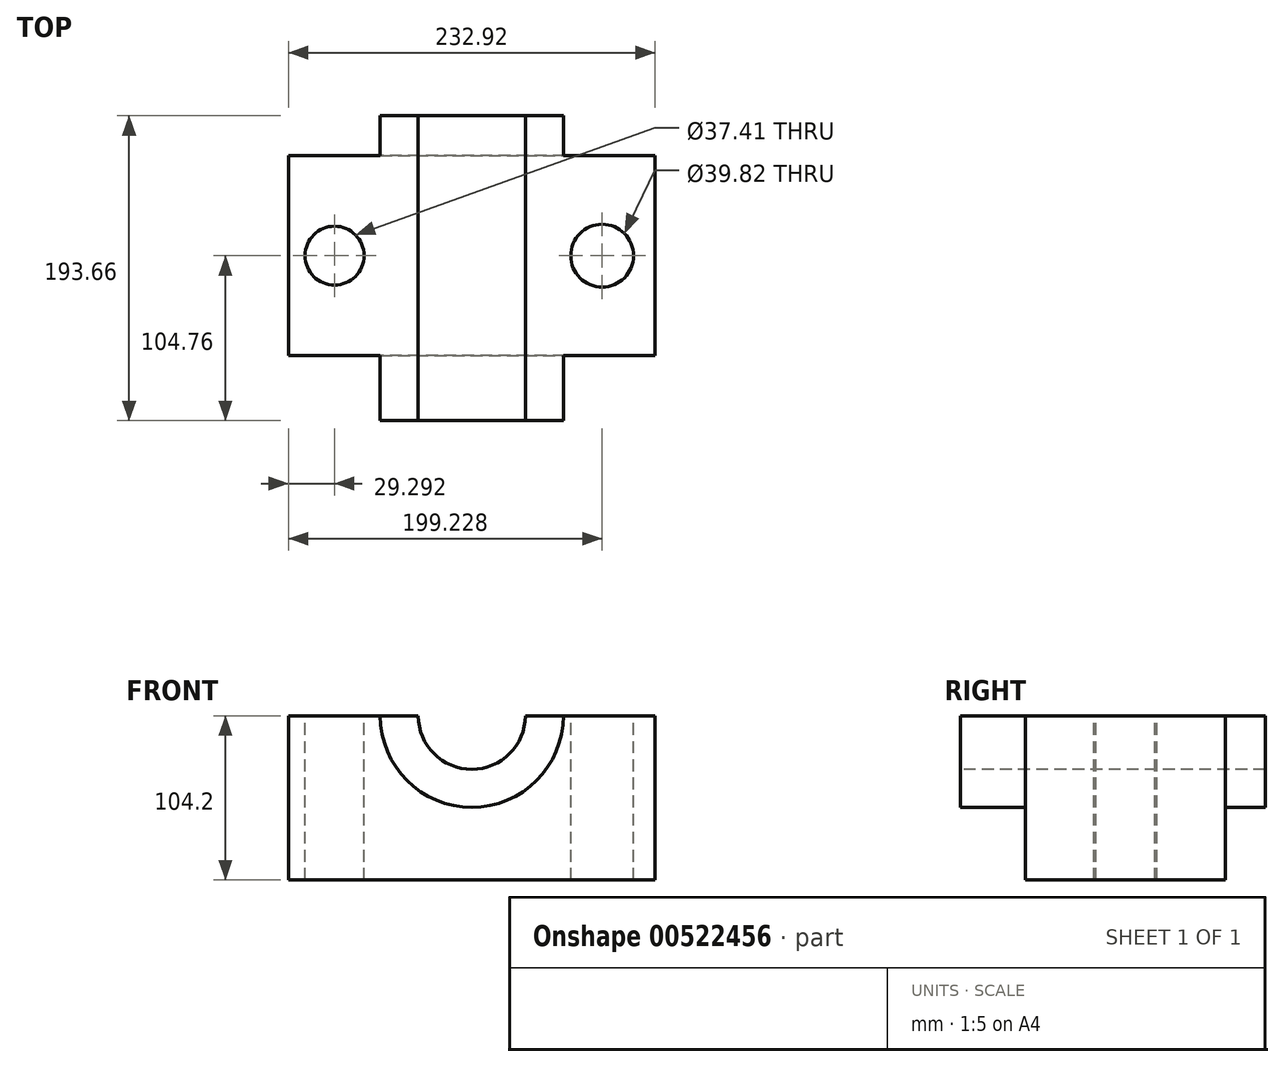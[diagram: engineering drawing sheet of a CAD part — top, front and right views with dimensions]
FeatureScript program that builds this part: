
annotation { "Feature Type Name" : "Feature", "Feature Type Description" : "" }
export const myFeature = defineFeature(function(context is Context, id is Id, definition is map)
    precondition{}
    {
        {
            var Q0;
            Q0=qCreatedBy(makeId("Front.planeOp"),FACE);
            var sketch = newSketch(context, id + "F0", { "sketchPlane" : qUnion([Q0])});
            skLineSegment(sketch, "E0.bottom", {"start": v(116.46, -52.1) * mm, "end": v(-116.46, -52.1) * mm});
            skLineSegment(sketch, "E0.top", {"start": v(116.46, 52.1) * mm, "end": v(-116.46, 52.1) * mm});
            skLineSegment(sketch, "E0.left", {"start": v(116.46, -52.1) * mm, "end": v(116.46, 52.1) * mm});
            skLineSegment(sketch, "E0.right", {"start": v(-116.46, -52.1) * mm, "end": v(-116.46, 52.1) * mm});
            skPoint(sketch, "E0.middle", {"position": v(0, 0) * mm});
            skSolve(sketch);
        }
        {
            var Q0;
            Q0 = qSketchRegion(id + "F0", true);
            extrude(context, id + "F1", {"entities" : qUnion([Q0]), "endBound" : BoundingType.SYMMETRIC, "oppositeDirection" : true, "depth" : 127 * mm, "offsetDistance" : 25.4 * mm});
        }
        {
            var Q0;
            Q0=makeQuery(id+"F1.opExtrude","CAP_FACE",FACE,{"disambiguationData":[OSD([sQuery(id+"F0.wireOp",EDGE,"E0.bottom"),sQuery(id+"F0.wireOp",EDGE,"E0.top"),sQuery(id+"F0.wireOp",EDGE,"E0.left"),sQuery(id+"F0.wireOp",EDGE,"E0.right")])],"isStart":true});
            var sketch = newSketch(context, id + "F2", { "sketchPlane" : qUnion([Q0])});
            skArc(sketch, "E1", {"start": v(-51.18, 52.1) * mm, "mid": v(0, 0.93) * mm, "end": v(51.18, 52.1) * mm});
            skArc(sketch, "E2", {"start": v(-34.02, 52.1) * mm, "mid": v(0, 18.08) * mm, "end": v(34.02, 52.1) * mm});
            skSolve(sketch);
        }
        {
            var Q0;
            Q0 = qSketchRegion(id + "F2", true);
            var Q1;
            {var subQ0=sQuery(id+"F2.wireOp",EDGE,"E2");Q1=makeQuery(id+"F2.imprint","IMPRINT",FACE,{"disambiguationData":[TD([[makeQuery(id+"F2.imprint","IMPRINT",EDGE,{"derivedFrom":subQ0}),1.0]])]});}
            extrude(context, id + "F3", {"entities" : qUnion([Q0, Q1]), "operationType" : NewBodyOperationType.REMOVE, "oppositeDirection" : true, "depth" : 296.93 * mm, "offsetDistance" : 25.4 * mm});
        }
        {
            var Q0;
            Q0=makeQuery(id+"F1.opExtrude","CAP_FACE",FACE,{"disambiguationData":[OSD([sQuery(id+"F0.wireOp",EDGE,"E0.bottom"),sQuery(id+"F0.wireOp",EDGE,"E0.top"),sQuery(id+"F0.wireOp",EDGE,"E0.left"),sQuery(id+"F0.wireOp",EDGE,"E0.right")])],"isStart":true});
            var sketch = newSketch(context, id + "F4", { "sketchPlane" : qUnion([Q0])});
            skArc(sketch, "E3", {"start": v(-58.18, 52.1) * mm, "mid": v(0, -6.08) * mm, "end": v(58.18, 52.1) * mm});
            skSolve(sketch);
        }
        {
            var Q0;
            {var subQ0=sQuery(id+"F4.wireOp",EDGE,"E3");Q0=makeQuery(id+"F4.imprint","IMPRINT",FACE,{"disambiguationData":[TD([[makeQuery(id+"F4.imprint","IMPRINT",EDGE,{"derivedFrom":subQ0}),1.0]])]});}
            extrude(context, id + "F5", {"entities" : qUnion([Q0]), "operationType" : NewBodyOperationType.ADD, "endBound" : BoundingType.SYMMETRIC, "depth" : 304.8 * mm, "offsetDistance" : 25.4 * mm});
        }
        {
            var Q0;
            Q0=qCreatedBy(makeId("Right.planeOp"),FACE);
            var sketch = newSketch(context, id + "F6", { "sketchPlane" : qUnion([Q0])});
            skLineSegment(sketch, "E4.bottom", {"start": v(-104.76, 71.05) * mm, "end": v(-229.58, 71.05) * mm});
            skLineSegment(sketch, "E4.top", {"start": v(-104.76, -42.63) * mm, "end": v(-229.58, -42.63) * mm});
            skLineSegment(sketch, "E4.left", {"start": v(-104.76, 71.05) * mm, "end": v(-104.76, -42.63) * mm});
            skLineSegment(sketch, "E4.right", {"start": v(-229.58, 71.05) * mm, "end": v(-229.58, -42.63) * mm});
            skSolve(sketch);
        }
        {
            var Q0;
            Q0 = qSketchRegion(id + "F6", true);
            extrude(context, id + "F7", {"entities" : qUnion([Q0]), "operationType" : NewBodyOperationType.REMOVE, "endBound" : BoundingType.SYMMETRIC, "oppositeDirection" : true, "depth" : 155.96 * mm, "offsetDistance" : 25.4 * mm});
        }
        {
            var Q0;
            {var subQ0=sQuery(id+"F0.wireOp",EDGE,"E0.right");var subQ2=sQuery(id+"F0.wireOp",EDGE,"E0.top");var subQ5=makeQuery(id+"F1.opExtrude","SWEPT_FACE",FACE,{"disambiguationData":[OSD([subQ2])]});var subQ6=sQuery(id+"F2.wireOp",EDGE,"E2");var subQ8=makeQuery(id+"F1.opExtrude","SWEPT_FACE",FACE,{"disambiguationData":[OSD([subQ0])]});var subQ9=makeQuery(id+"F3.boolean.opBoolean","SPLIT",EDGE,{"disambiguationData":[TD([subQ8])],"derivedFrom":makeQuery(id+"F1.opExtrude","CAP_EDGE",EDGE,{"disambiguationData":[OSD([subQ2])],"isStart":true})});Q0=makeQuery(id+"F5.boolean.opBoolean","MERGE",FACE,{"derivedFrom":[makeQuery(id+"F3.boolean.opBoolean","SPLIT",FACE,{"disambiguationData":[TD([subQ8])],"derivedFrom":subQ5}),makeQuery(id+"F5.opExtrude","SWEPT_FACE",FACE,{"disambiguationData":[OSD([subQ2]),TDD([makeQuery(id+"F4.imprint","IMPRINT",EDGE,{"disambiguationData":[TD([[makeQuery(id+"F4.imprint","INTERSECT",VERTEX,{"derivedFrom":[makeQuery(id+"F3.boolean.opBoolean","COPY",EDGE,{"derivedFrom":makeQuery(id+"F3.opExtrude","CAP_EDGE",EDGE,{"disambiguationData":[OSD([subQ6])],"isStart":true})}),subQ9]}),-1.0]])],"derivedFrom":subQ9})])]})]});}
            var sketch = newSketch(context, id + "F8", { "sketchPlane" : qUnion([Q0])});
            skCircle(sketch, "E5", {"center": v(-87.17, 0) * mm, "radius": 18.7 * mm});
            skCircle(sketch, "E6", {"center": v(82.77, 0) * mm, "radius": 19.9 * mm});
            skSolve(sketch);
        }
        {
            var Q0;
            Q0 = qSketchRegion(id + "F8", true);
            extrude(context, id + "F9", {"entities" : qUnion([Q0]), "operationType" : NewBodyOperationType.REMOVE, "oppositeDirection" : true, "depth" : 1270 * mm, "offsetDistance" : 25.4 * mm});
        }
    });
